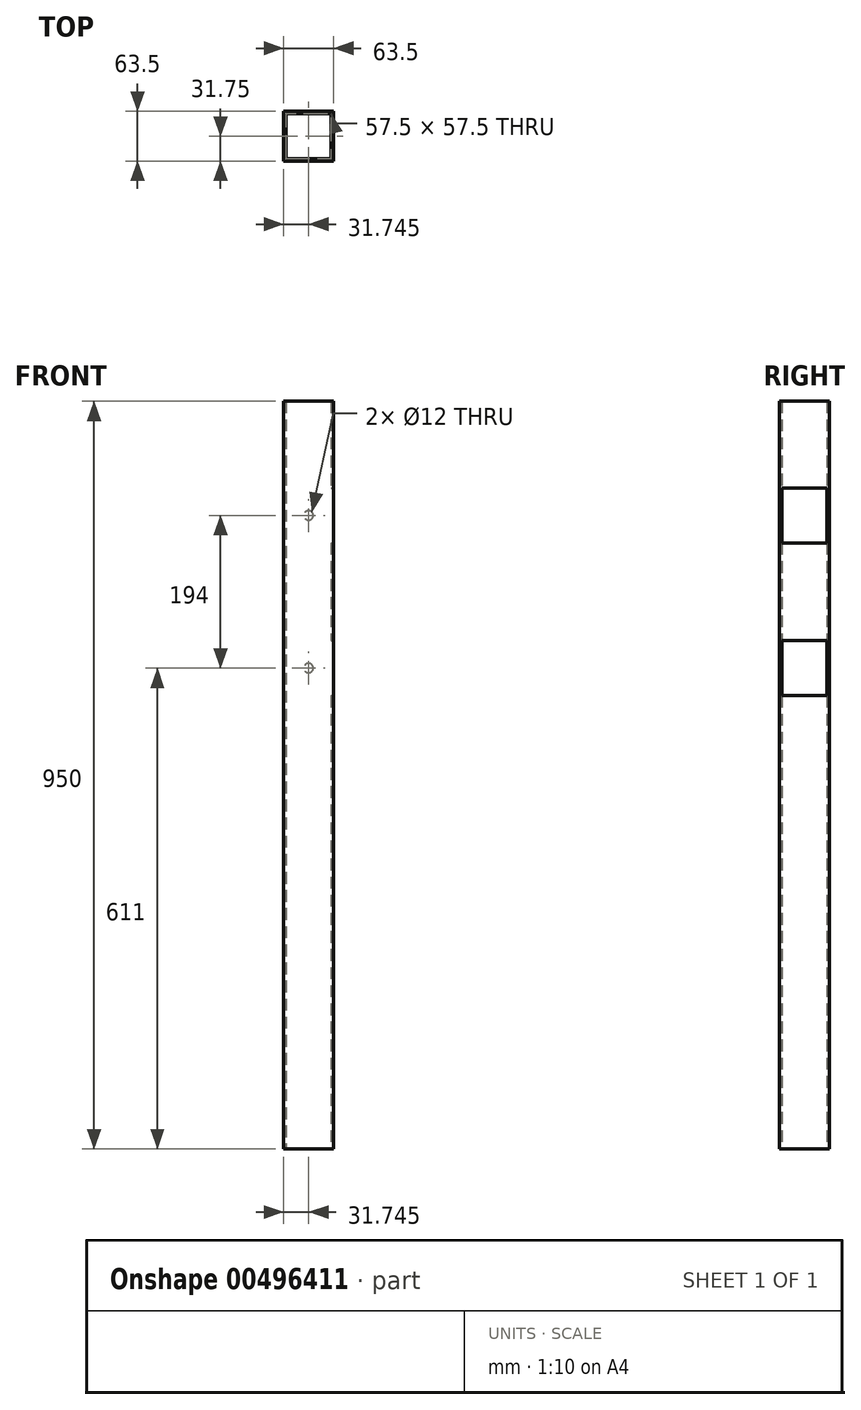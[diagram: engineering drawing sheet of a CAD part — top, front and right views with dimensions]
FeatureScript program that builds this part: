
annotation { "Feature Type Name" : "Feature", "Feature Type Description" : "" }
export const myFeature = defineFeature(function(context is Context, id is Id, definition is map)
    precondition{}
    {
        {
            var Q0;
            Q0=qCreatedBy(makeId("Top.planeOp"),FACE);
            var sketch = newSketch(context, id + "F0", { "sketchPlane" : qUnion([Q0])});
            skLineSegment(sketch, "E0.bottom", {"start": v(-24.13, 26.04) * mm, "end": v(39.37, 26.04) * mm});
            skLineSegment(sketch, "E0.top", {"start": v(-24.13, -37.46) * mm, "end": v(39.37, -37.46) * mm});
            skLineSegment(sketch, "E0.left", {"start": v(-24.13, 26.04) * mm, "end": v(-24.13, -37.46) * mm});
            skLineSegment(sketch, "E0.right", {"start": v(39.37, 26.04) * mm, "end": v(39.37, -37.46) * mm});
            skLineSegment(sketch, "E1.bottom", {"start": v(-21.13, 23.04) * mm, "end": v(36.37, 23.04) * mm});
            skLineSegment(sketch, "E1.top", {"start": v(-21.13, -34.46) * mm, "end": v(36.37, -34.46) * mm});
            skLineSegment(sketch, "E1.left", {"start": v(-21.13, 23.04) * mm, "end": v(-21.13, -34.46) * mm});
            skLineSegment(sketch, "E1.right", {"start": v(36.37, 23.04) * mm, "end": v(36.37, -34.46) * mm});
            skSolve(sketch);
        }
        {
            var Q0;
            Q0=qSketchRegion(id+"F0",true);
            extrude(context, id + "F1", {"entities" : qUnion([Q0]), "depth" : 950 * mm});
        }
        {
            var Q0;
            Q0=makeQuery(id+"F1.opExtrude","SWEPT_FACE",FACE,{"disambiguationData":[OSD([sQuery(id+"F0.wireOp",EDGE,"E0.right")])]});
            var sketch = newSketch(context, id + "F2", { "sketchPlane" : qUnion([Q0])});
            skLineSegment(sketch, "E2.bottom", {"start": v(23.04, 840) * mm, "end": v(-34.46, 840) * mm});
            skLineSegment(sketch, "E2.top", {"start": v(23.04, 770) * mm, "end": v(-34.46, 770) * mm});
            skLineSegment(sketch, "E2.left", {"start": v(23.04, 840) * mm, "end": v(23.04, 770) * mm});
            skLineSegment(sketch, "E2.right", {"start": v(-34.46, 840) * mm, "end": v(-34.46, 770) * mm});
            skSolve(sketch);
        }
        {
            var Q0;
            Q0=qSketchRegion(id+"F2",true);
            extrude(context, id + "F3", {"entities" : qUnion([Q0]), "operationType" : NewBodyOperationType.REMOVE, "oppositeDirection" : true, "depth" : 3 * mm});
        }
        {
            var Q0;
            Q0=makeQuery(id+"F1.opExtrude","SWEPT_FACE",FACE,{"disambiguationData":[OSD([sQuery(id+"F0.wireOp",EDGE,"E0.right")])]});
            var sketch = newSketch(context, id + "F4", { "sketchPlane" : qUnion([Q0])});
            skLineSegment(sketch, "E3.bottom", {"start": v(23.04, 646) * mm, "end": v(-34.46, 646) * mm});
            skLineSegment(sketch, "E3.top", {"start": v(23.04, 576) * mm, "end": v(-34.46, 576) * mm});
            skLineSegment(sketch, "E3.left", {"start": v(23.04, 646) * mm, "end": v(23.04, 576) * mm});
            skLineSegment(sketch, "E3.right", {"start": v(-34.46, 646) * mm, "end": v(-34.46, 576) * mm});
            skSolve(sketch);
        }
        {
            var Q0;
            Q0=qSketchRegion(id+"F4",true);
            extrude(context, id + "F5", {"entities" : qUnion([Q0]), "operationType" : NewBodyOperationType.REMOVE, "oppositeDirection" : true, "depth" : 3 * mm});
        }
        {
            var Q0;
            Q0=makeQuery(id+"F1.opExtrude","SWEPT_FACE",FACE,{"disambiguationData":[OSD([sQuery(id+"F0.wireOp",EDGE,"E0.right")])]});
            var sketch = newSketch(context, id + "F6", { "sketchPlane" : qUnion([Q0])});
            skSolve(sketch);
        }
        {
            var Q0;
            Q0=qSketchRegion(id+"F4",true);
            extrude(context, id + "F7", {"entities" : qUnion([Q0]), "depth" : 3 * mm});
        }
        {
            var Q0;
            Q0=makeQuery(id+"F7.opExtrude","CAP_FACE",FACE,{"disambiguationData":[OSD([sQuery(id+"F4.wireOp",EDGE,"E3.bottom"),sQuery(id+"F4.wireOp",EDGE,"E3.top"),sQuery(id+"F4.wireOp",EDGE,"E3.left"),sQuery(id+"F4.wireOp",EDGE,"E3.right")])],"isStart":false});
            extrude(context, id + "F8", {"entities" : qUnion([Q0]), "operationType" : NewBodyOperationType.REMOVE, "oppositeDirection" : true, "depth" : 3 * mm});
        }
        {
            var Q0;
            Q0=makeQuery(id+"F1.opExtrude","SWEPT_FACE",FACE,{"disambiguationData":[OSD([sQuery(id+"F0.wireOp",EDGE,"E0.bottom")])]});
            var sketch = newSketch(context, id + "F9", { "sketchPlane" : qUnion([Q0])});
            skCircle(sketch, "E4", {"center": v(-7.62, 805) * mm, "radius": 6 * mm});
            skSolve(sketch);
        }
        {
            var Q0;
            Q0=qSketchRegion(id+"F9",true);
            extrude(context, id + "F10", {"entities" : qUnion([Q0]), "operationType" : NewBodyOperationType.REMOVE, "oppositeDirection" : true, "depth" : 3 * mm});
        }
        {
            var Q0;
            Q0=makeQuery(id+"F1.opExtrude","SWEPT_FACE",FACE,{"disambiguationData":[OSD([sQuery(id+"F0.wireOp",EDGE,"E0.bottom")])]});
            var sketch = newSketch(context, id + "F11", { "sketchPlane" : qUnion([Q0])});
            skCircle(sketch, "E5", {"center": v(-7.62, 611) * mm, "radius": 6 * mm});
            skSolve(sketch);
        }
        {
            var Q0;
            Q0=qSketchRegion(id+"F11",true);
            extrude(context, id + "F12", {"entities" : qUnion([Q0]), "operationType" : NewBodyOperationType.REMOVE, "oppositeDirection" : true, "depth" : 3 * mm});
        }
    });
